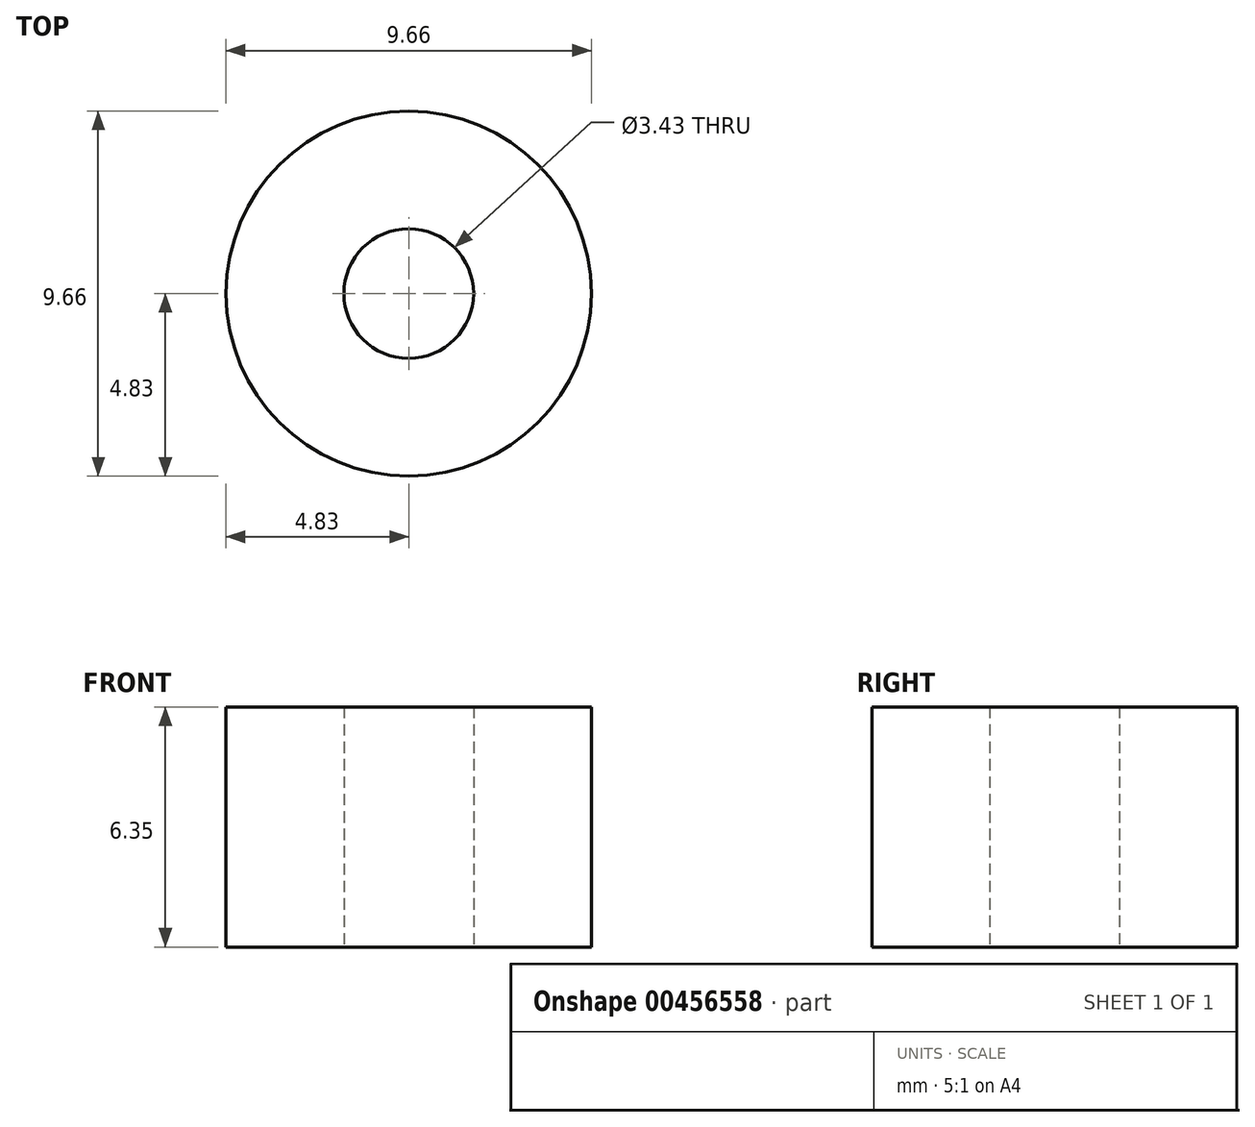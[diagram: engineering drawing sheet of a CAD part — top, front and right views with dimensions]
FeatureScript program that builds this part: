
annotation { "Feature Type Name" : "Feature", "Feature Type Description" : "" }
export const myFeature = defineFeature(function(context is Context, id is Id, definition is map)
    precondition{}
    {
        {
            var Q0;
            Q0=qCreatedBy(makeId("Top.planeOp"),FACE);
            var sketch = newSketch(context, id + "F0", { "sketchPlane" : qUnion([Q0])});
            skCircle(sketch, "E0", {"center": v(0, 0) * mm, "radius": 1.71 * mm});
            skCircle(sketch, "E1", {"center": v(0, 0) * mm, "radius": 4.83 * mm});
            skSolve(sketch);
        }
        {
            var Q0;
            Q0=makeQuery(id+"F0.imprint","IMPRINT",FACE,{"disambiguationData":[TD([[makeQuery(id+"F0.imprint","IMPRINT",EDGE,{"derivedFrom":sQuery(id+"F0.wireOp",EDGE,"E0")}),-1.0]])]});
            extrude(context, id + "F1", {"entities" : qUnion([Q0]), "depth" : 6.35 * mm});
        }
    });
